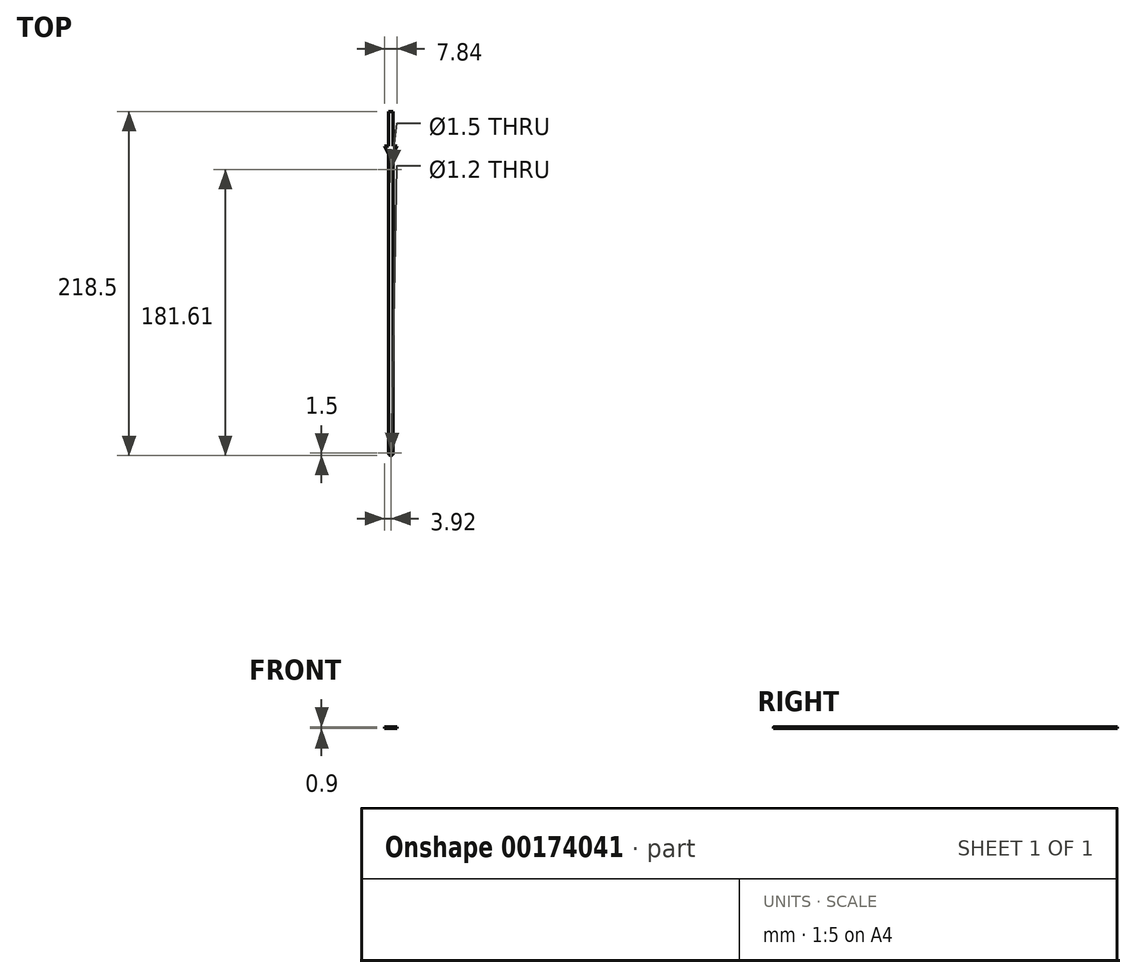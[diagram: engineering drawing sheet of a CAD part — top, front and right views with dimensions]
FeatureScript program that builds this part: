
annotation { "Feature Type Name" : "Feature", "Feature Type Description" : "" }
export const myFeature = defineFeature(function(context is Context, id is Id, definition is map)
    precondition{}
    {
        {
            var Q0;
            Q0=qCreatedBy(makeId("Top.planeOp"),FACE);
            var sketch = newSketch(context, id + "F0", { "sketchPlane" : qUnion([Q0])});
            skLineSegment(sketch, "E0.bottom", {"start": v(-1.5, 108.5) * mm, "end": v(1.5, 108.5) * mm});
            skLineSegment(sketch, "E0.top", {"start": v(-1.5, -108.5) * mm, "end": v(1.5, -108.5) * mm, "construction": true});
            skLineSegment(sketch, "E0.left", {"start": v(-1.5, 108.5) * mm, "end": v(-1.5, -108.5) * mm});
            skLineSegment(sketch, "E0.right", {"start": v(1.5, 108.5) * mm, "end": v(1.5, -108.5) * mm});
            skPoint(sketch, "E1", {"position": v(0, 108.5) * mm});
            skPoint(sketch, "E2", {"position": v(-1.5, 0) * mm});
            skLineSegment(sketch, "E3.bottom", {"start": v(-3.92, 86.5) * mm, "end": v(3.92, 86.5) * mm});
            skLineSegment(sketch, "E3.top", {"start": v(0, 78.26) * mm, "end": v(3.92, 86.5) * mm});
            skLineSegment(sketch, "E3.left", {"start": v(-3.92, 86.5) * mm, "end": v(0, 78.26) * mm});
            skPoint(sketch, "E4", {"position": v(0, 86.5) * mm});
            skCircle(sketch, "E5", {"center": v(0, 71.6) * mm, "radius": 0.75 * mm});
            skCircle(sketch, "E6", {"center": v(0, -108.5) * mm, "radius": 0.63 * mm, "construction": true});
            skCircle(sketch, "E7", {"center": v(0, -108.5) * mm, "radius": 1.5 * mm});
            skSolve(sketch);
        }
        {
            var Q0;
            Q0 = qSketchRegion(id + "F0", true);
            extrude(context, id + "F1", {"entities" : qUnion([Q0]), "depth" : 0.9 * mm});
        }
        {
            var Q0;
            Q0=qCreatedBy(makeId("Top.planeOp"),FACE);
            var sketch = newSketch(context, id + "F2", { "sketchPlane" : qUnion([Q0])});
            skPoint(sketch, "E8.0", {"position": v(0, -108.5) * mm});
            skCircle(sketch, "E9", {"center": v(0, -108.5) * mm, "radius": 0.6 * mm});
            skSolve(sketch);
        }
        {
            var Q0;
            Q0 = qSketchRegion(id + "F2", true);
            extrude(context, id + "F3", {"entities" : qUnion([Q0]), "operationType" : NewBodyOperationType.REMOVE, "endBound" : BoundingType.THROUGH_ALL, "depth" : 25 * mm});
        }
    });
